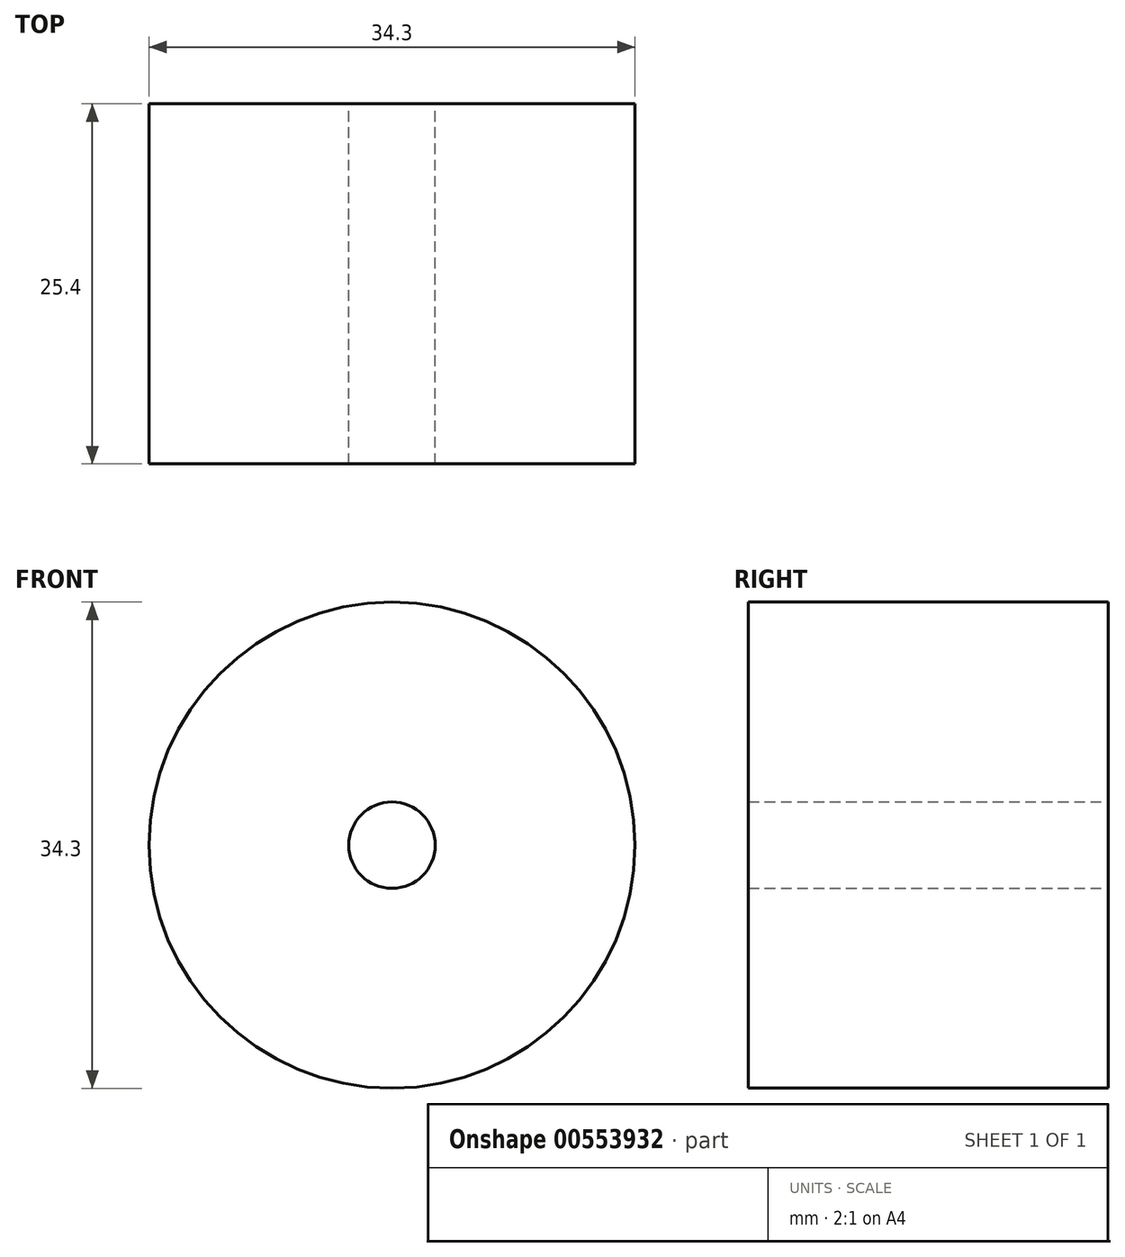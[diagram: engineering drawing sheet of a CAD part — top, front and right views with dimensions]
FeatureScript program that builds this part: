
annotation { "Feature Type Name" : "Feature", "Feature Type Description" : "" }
export const myFeature = defineFeature(function(context is Context, id is Id, definition is map)
    precondition{}
    {
        {
            var Q0;
            Q0=qCreatedBy(makeId("Front.planeOp"),FACE);
            var sketch = newSketch(context, id + "F0", { "sketchPlane" : qUnion([Q0])});
            skCircle(sketch, "E0", {"center": v(0, 0) * mm, "radius": 17.15 * mm});
            skCircle(sketch, "E1", {"center": v(0, 0) * mm, "radius": 3.05 * mm});
            skSolve(sketch);
        }
        {
            var Q0;
            Q0=makeQuery(id+"F0.imprint","IMPRINT",FACE,{"disambiguationData":[TD([[makeQuery(id+"F0.imprint","IMPRINT",EDGE,{"derivedFrom":sQuery(id+"F0.wireOp",EDGE,"E0")}),1.0]])]});
            extrude(context, id + "F1", {"entities" : qUnion([Q0]), "depth" : 25.4 * mm, "offsetDistance" : 25.4 * mm});
        }
    });
